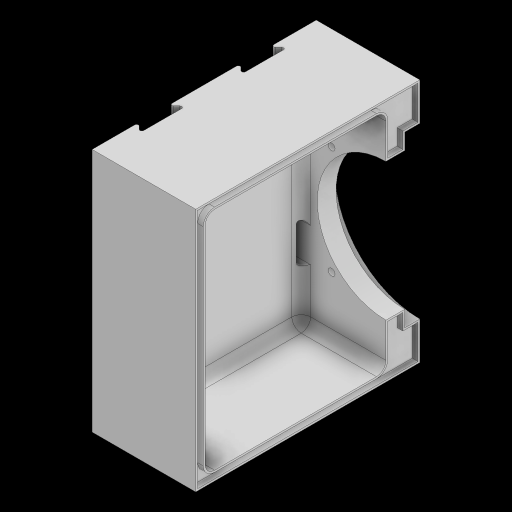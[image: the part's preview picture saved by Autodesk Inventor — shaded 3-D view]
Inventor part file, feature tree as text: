
AUTODESK INVENTOR PART (.ipt)
format: ipt  version: 2023 (Build 270158000, 158)  size: 363,520 bytes
history: native  units: in
note: dims shown in document units (in); Inventor stores cm internally (conversion verified against a paired STEP export)
features: extrude x10, sketch x10, projected_geometry x5, plane x2, fillet x2, split x1
ambient origin geometry x8: Origin, YZ Plane, XZ Plane, XY Plane, X Axis, Y Axis, Z Axis, Center Point
bodies: Solid1 (feature_tree)
feature tree (30):
  extrude  "Extrusion1"  Depth=3.937in
  sketch  "Sketch2"  dims[d2=5.1181in d3=0.0in d4=0.315in d5=0.0in]
  extrude  "Extrusion2"  Depth=0.315in TaperAngle=0.0deg
  extrude  "Extrusion3"  Depth=3.937in
  plane  "Work Plane1"
  extrude  "Extrusion4"  Depth=5.1181in
  fillet  "Fillet1"  Radius=5.1181in
  sketch  "Sketch8"  dims[d8=1.9685in d9=2.5591in d10=5.1181in]
  extrude  "Extrusion10"  Depth=0.1496in
  extrude  "Extrusion11"  [1 undecoded]
  fillet  "Fillet2"  Radius=0.1969in
  extrude  "Extrusion12"  Depth=0.1969in
  extrude  "Extrusion13"  Depth=3.5433in TaperAngle=0.0deg
  extrude  "Extrusion14"  Depth=0.1969in TaperAngle=0.0deg
  plane  "Work Plane2"
  split  "Split1"
  extrude  "Extrusion15"  Depth=0.1181in TaperAngle=0.0deg
  sketch  "Sketch1"  dims[d0=4.685in d1=3.937in]
  sketch  "Sketch3"  dims[d6=3.5433in d7=3.937in]
  projected_geometry  "Projected Loop1"
  sketch  "Sketch10"  dims[d11=2.874in d12=0.1496in]
  projected_geometry  "Projected Loop2"
  sketch  "Sketch12"  dims[d13=0.7087in d14=0.0in d15=-0.1969in d16=0.1969in]
  projected_geometry  "Projected Loop4"
  sketch  "Sketch13"  dims[d17=0.1969in d18=0.1969in]
  sketch  "Sketch14"  dims[d19=3.5433in d20=0.0in d21=3.5433in d22=0.0in]
  sketch  "Sketch15"  dims[d23=0.1969in d74=0.1969in d75=0.0in]
  sketch  "Sketch19"  dims[d82=4.685in d84=5.0in d85=0.0in d86=0.1969in d87=45.0deg d88=45.0deg d90=45.0deg d91=45.0deg d92=0.7874in d93=0.9843in d94=0.7874in d95=0.9843in d96=0.0394in d97=3.3465in d98=4.3307in d99=3.5433in d100=0.0984in d101=0.1575in d102=0.1693in d103=0.1417in d104=0.1969in d105=0.1693in d107=4.7244in d108=0.1969in d109=0.1575in d110=0.1417in d111=0.1969in d112=0.1417in d113=0.1969in d114=0.1417in d115=0.1969in d116=0.1181in d117=0.0in d118=0.7087in d119=0.1181in d121=0.7087in d122=1.3386in d123=0.7874in d124=0.0in d125=45.0deg d126=2.874in d129=3.5433in d130=0.1673in d131=0.1417in d135=0.1417in d136=0.1417in d137=0.1417in d138=1.5748in d139=0.0in d141=0.0394in d142=0.1181in d143=0.0in d144=0.0344in]
  projected_geometry  "Projected Loop6"
  projected_geometry  "Project Cut Edges1"
note: 1 required parameter value undecoded (feature->parameter linkage not recoverable at this tier; creation-order binding heuristic only, values carry confidence <= 0.55)
